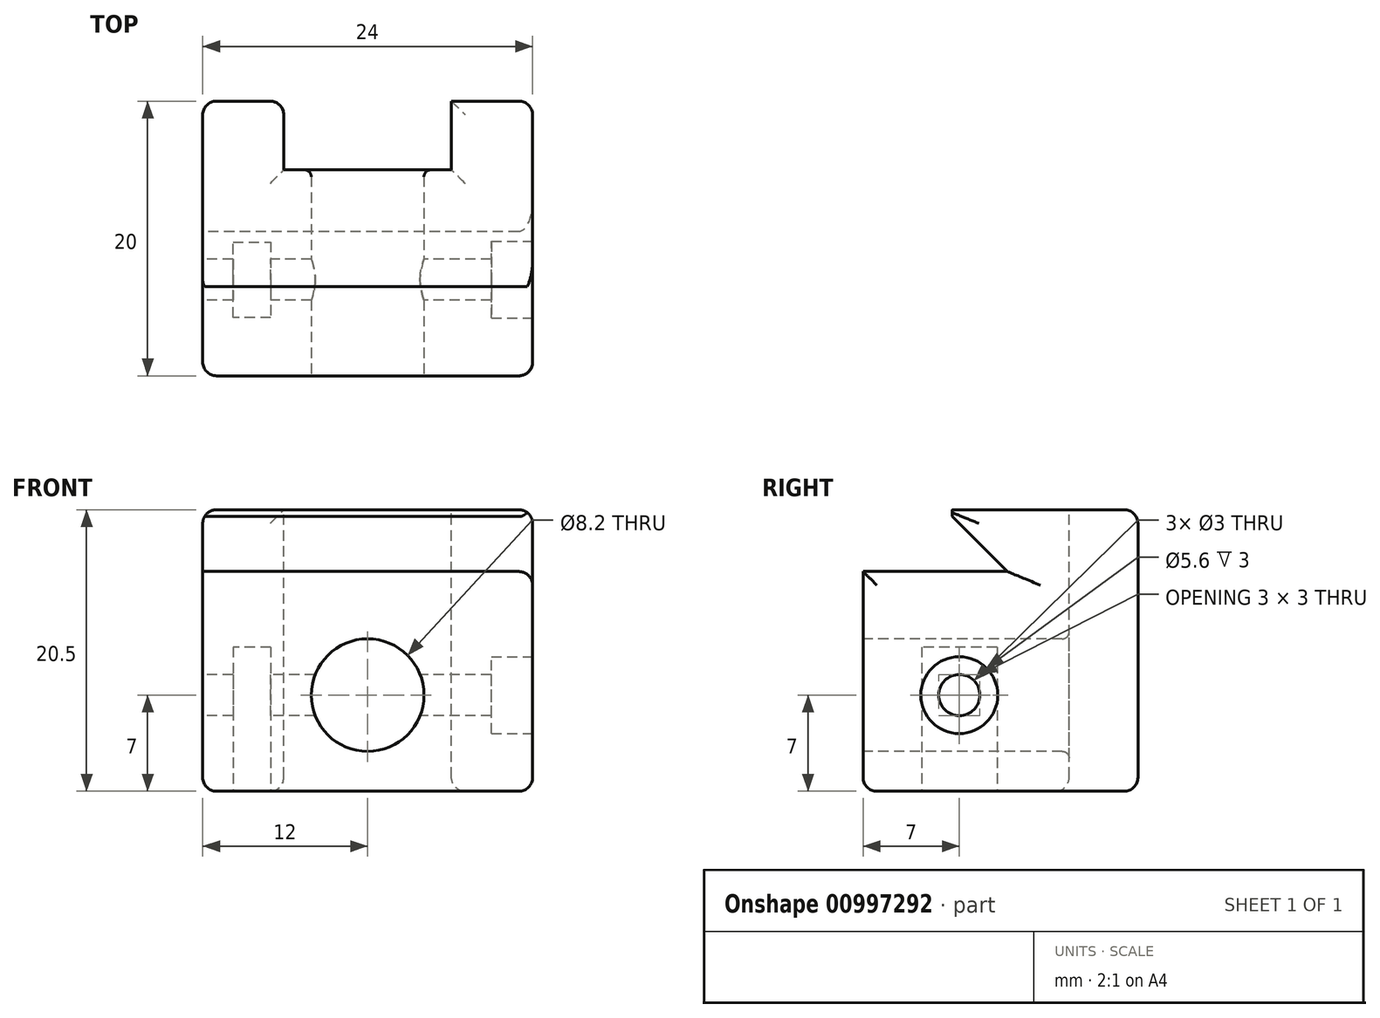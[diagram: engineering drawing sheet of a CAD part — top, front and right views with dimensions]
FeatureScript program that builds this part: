
annotation { "Feature Type Name" : "Feature", "Feature Type Description" : "" }
export const myFeature = defineFeature(function(context is Context, id is Id, definition is map)
    precondition{}
    {
        {
            var Q0;
            Q0=qCreatedBy(makeId("Top.planeOp"),FACE);
            var sketch = newSketch(context, id + "F0", { "sketchPlane" : qUnion([Q0])});
            skLineSegment(sketch, "E0.bottom", {"start": v(12, 10) * mm, "end": v(-12, 10) * mm});
            skLineSegment(sketch, "E0.top", {"start": v(12, -10) * mm, "end": v(-12, -10) * mm});
            skLineSegment(sketch, "E0.left", {"start": v(12, 10) * mm, "end": v(12, -10) * mm});
            skLineSegment(sketch, "E0.right", {"start": v(-12, 10) * mm, "end": v(-12, -10) * mm});
            skPoint(sketch, "E0.middle", {"position": v(0, 0) * mm});
            skSolve(sketch);
        }
        {
            var Q0;
            Q0 = qSketchRegion(id + "F0", true);
            extrude(context, id + "F1", {"entities" : qUnion([Q0]), "depth" : 18.5 * mm, "offsetDistance" : 25 * mm});
        }
        {
            var Q0;
            Q0=makeQuery(id+"F1.opExtrude","SWEPT_FACE",FACE,{"disambiguationData":[OSD([sQuery(id+"F0.wireOp",EDGE,"E0.right")])]});
            var sketch = newSketch(context, id + "F2", { "sketchPlane" : qUnion([Q0])});
            skLineSegment(sketch, "E1", {"start": v(10, 0) * mm, "end": v(10, 14) * mm, "construction": true});
            skLineSegment(sketch, "E2", {"start": v(10, 14) * mm, "end": v(-0.5, 14) * mm});
            skLineSegment(sketch, "E3", {"start": v(-10, 18.5) * mm, "end": v(4, 18.5) * mm, "construction": true});
            skLineSegment(sketch, "E4", {"start": v(3.5, 18) * mm, "end": v(-0.5, 14) * mm});
            skLineSegment(sketch, "E5", {"start": v(4, 18.5) * mm, "end": v(3.5, 18.5) * mm, "construction": true});
            skLineSegment(sketch, "E6", {"start": v(3.5, 18.5) * mm, "end": v(3.5, 18) * mm});
            skLineSegment(sketch, "E7", {"start": v(10, 0) * mm, "end": v(10, 5) * mm, "construction": true});
            skLineSegment(sketch, "E8", {"start": v(10, 5) * mm, "end": v(3, 5) * mm, "construction": true});
            skCircle(sketch, "E9", {"center": v(3, 5) * mm, "radius": 1.5 * mm});
            skSolve(sketch);
        }
        {
            var Q0;
            {var subQ4=sQuery(id+"F2.wireOp",EDGE,"E2");Q0=makeQuery(id+"F2.imprint","IMPRINT",FACE,{"disambiguationData":[TD([[makeQuery(id+"F2.imprint","IMPRINT",EDGE,{"derivedFrom":subQ4}),-1.0]])]});}
            var Q1;
            Q1=makeQuery(id+"F2.imprint","IMPRINT",FACE,{"disambiguationData":[TD([[makeQuery(id+"F2.imprint","IMPRINT",EDGE,{"derivedFrom":sQuery(id+"F2.wireOp",EDGE,"E9")}),1.0]])]});
            extrude(context, id + "F3", {"entities" : qUnion([Q0, Q1]), "operationType" : NewBodyOperationType.REMOVE, "oppositeDirection" : true, "depth" : 25 * mm, "offsetDistance" : 25 * mm});
        }
        {
            var Q0;
            Q0=makeQuery(id+"F1.opExtrude","CAP_FACE",FACE,{"disambiguationData":[OSD([sQuery(id+"F0.wireOp",EDGE,"E0.bottom"),sQuery(id+"F0.wireOp",EDGE,"E0.top"),sQuery(id+"F0.wireOp",EDGE,"E0.left"),sQuery(id+"F0.wireOp",EDGE,"E0.right")])],"isStart":true});
            extrude(context, id + "F4", {"entities" : qUnion([Q0]), "operationType" : NewBodyOperationType.ADD, "depth" : 2 * mm, "offsetDistance" : 25 * mm});
        }
        {
            var Q0;
            {var subQ0=sQuery(id+"F0.wireOp",EDGE,"E0.top");Q0=makeQuery(id+"F4.boolean.opBoolean","MERGE",FACE,{"derivedFrom":[makeQuery(id+"F1.opExtrude","SWEPT_FACE",FACE,{"disambiguationData":[OSD([subQ0])]}),makeQuery(id+"F4.opExtrude","SWEPT_FACE",FACE,{"disambiguationData":[OSD([subQ0])]})]});}
            var sketch = newSketch(context, id + "F5", { "sketchPlane" : qUnion([Q0])});
            skLineSegment(sketch, "E10", {"start": v(0, -2) * mm, "end": v(0, 12) * mm, "construction": true});
            skCircle(sketch, "E11", {"center": v(0, 5) * mm, "radius": 4.1 * mm});
            skSolve(sketch);
        }
        {
            var Q0;
            Q0=makeQuery(id+"F5.imprint","IMPRINT",FACE,{"disambiguationData":[TD([[makeQuery(id+"F5.imprint","IMPRINT",EDGE,{"derivedFrom":sQuery(id+"F5.wireOp",EDGE,"E11")}),1.0]])]});
            extrude(context, id + "F6", {"entities" : qUnion([Q0]), "operationType" : NewBodyOperationType.REMOVE, "oppositeDirection" : true, "depth" : 25 * mm, "offsetDistance" : 25 * mm});
        }
        {
            var Q0;
            Q0=makeQuery(id+"F1.opExtrude","CAP_FACE",FACE,{"disambiguationData":[OSD([sQuery(id+"F0.wireOp",EDGE,"E0.bottom"),sQuery(id+"F0.wireOp",EDGE,"E0.top"),sQuery(id+"F0.wireOp",EDGE,"E0.left"),sQuery(id+"F0.wireOp",EDGE,"E0.right")])],"isStart":false});
            var sketch = newSketch(context, id + "F7", { "sketchPlane" : qUnion([Q0])});
            skLineSegment(sketch, "E12", {"start": v(0, 10) * mm, "end": v(6.1, 10) * mm, "construction": true});
            skLineSegment(sketch, "E13", {"start": v(0, 10) * mm, "end": v(-6.1, 10) * mm, "construction": true});
            skLineSegment(sketch, "E14", {"start": v(-6.1, 10) * mm, "end": v(-6.1, 5) * mm});
            skLineSegment(sketch, "E15", {"start": v(-6.1, 5) * mm, "end": v(6.1, 5) * mm});
            skLineSegment(sketch, "E16", {"start": v(6.1, 5) * mm, "end": v(6.1, 10) * mm});
            skSolve(sketch);
        }
        {
            var Q0;
            {var subQ0=sQuery(id+"F7.wireOp",EDGE,"E14");Q0=makeQuery(id+"F7.imprint","IMPRINT",FACE,{"disambiguationData":[TD([[makeQuery(id+"F7.imprint","IMPRINT",EDGE,{"derivedFrom":subQ0}),1.0]])]});}
            extrude(context, id + "F8", {"entities" : qUnion([Q0]), "operationType" : NewBodyOperationType.REMOVE, "oppositeDirection" : true, "depth" : 25 * mm, "offsetDistance" : 25 * mm});
        }
        {
            var Q0;
            {var subQ0=sQuery(id+"F0.wireOp",EDGE,"E0.left");Q0=makeQuery(id+"F4.boolean.opBoolean","MERGE",FACE,{"derivedFrom":[makeQuery(id+"F1.opExtrude","SWEPT_FACE",FACE,{"disambiguationData":[OSD([subQ0])]}),makeQuery(id+"F4.opExtrude","SWEPT_FACE",FACE,{"disambiguationData":[OSD([subQ0])]})]});}
            var sketch = newSketch(context, id + "F9", { "sketchPlane" : qUnion([Q0])});
            skCircle(sketch, "E17", {"center": v(-3, 5) * mm, "radius": 2.8 * mm});
            skSolve(sketch);
        }
        {
            var Q0;
            Q0=makeQuery(id+"F9.imprint","IMPRINT",FACE,{"disambiguationData":[TD([[makeQuery(id+"F9.imprint","IMPRINT",EDGE,{"derivedFrom":sQuery(id+"F9.wireOp",EDGE,"E17")}),1.0]])]});
            extrude(context, id + "F10", {"entities" : qUnion([Q0]), "operationType" : NewBodyOperationType.REMOVE, "oppositeDirection" : true, "depth" : 3 * mm, "offsetDistance" : 25 * mm});
        }
        {
            var Q0;
            Q0=makeQuery(id+"F4.opExtrude","CAP_FACE",FACE,{"disambiguationData":[OSD([sQuery(id+"F0.wireOp",EDGE,"E0.bottom"),sQuery(id+"F0.wireOp",EDGE,"E0.top"),sQuery(id+"F0.wireOp",EDGE,"E0.left"),sQuery(id+"F0.wireOp",EDGE,"E0.right")])],"isStart":false});
            var sketch = newSketch(context, id + "F11", { "sketchPlane" : qUnion([Q0])});
            skLineSegment(sketch, "E18", {"start": v(0, 10) * mm, "end": v(0, 3) * mm, "construction": true});
            skLineSegment(sketch, "E19", {"start": v(0, 3) * mm, "end": v(-7.05, 3) * mm, "construction": true});
            skLineSegment(sketch, "E20", {"start": v(-7.05, 3) * mm, "end": v(-7.05, 5.75) * mm});
            skLineSegment(sketch, "E21", {"start": v(-7.05, 5.75) * mm, "end": v(-9.8, 5.75) * mm});
            skLineSegment(sketch, "E22", {"start": v(-9.8, 5.75) * mm, "end": v(-9.8, 0.25) * mm});
            skLineSegment(sketch, "E23", {"start": v(-9.8, 0.25) * mm, "end": v(-7.05, 0.25) * mm});
            skLineSegment(sketch, "E24", {"start": v(-7.05, 0.25) * mm, "end": v(-7.05, 3) * mm});
            skLineSegment(sketch, "E25", {"start": v(-9.8, 3) * mm, "end": v(-12, 3) * mm, "construction": true});
            skSolve(sketch);
        }
        {
            var Q0;
            Q0=makeQuery(id+"F11.imprint","IMPRINT",FACE,{"disambiguationData":[TD([[makeQuery(id+"F11.imprint","IMPRINT",EDGE,{"derivedFrom":sQuery(id+"F11.wireOp",EDGE,"E20")}),1.0]])]});
            extrude(context, id + "F12", {"entities" : qUnion([Q0]), "operationType" : NewBodyOperationType.REMOVE, "oppositeDirection" : true, "depth" : 10.5 * mm, "offsetDistance" : 25 * mm});
        }
        {
            var Q0;
            Q0=makeQuery(id+"F3.boolean.opBoolean","COPY",EDGE,{"derivedFrom":makeQuery(id+"F3.opExtrude","CAP_EDGE",EDGE,{"disambiguationData":[OSD([sQuery(id+"F2.wireOp",EDGE,"E2")])],"isStart":true})});
            var Q1;
            Q1=makeQuery(id+"F3.boolean.opBoolean","COPY",EDGE,{"derivedFrom":makeQuery(id+"F3.opExtrude","SWEPT_EDGE",EDGE,{"disambiguationData":[OSD([sQuery(id+"F0.wireOp",EDGE,"E0.top"),sQuery(id+"F0.wireOp",EDGE,"E0.right"),sQuery(id+"F2.wireOp",EDGE,"E2")])]})});
            var Q2;
            Q2=makeQuery(id+"F3.boolean.opBoolean","INTERSECT",EDGE,{"derivedFrom":[makeQuery(id+"F1.opExtrude","SWEPT_FACE",FACE,{"disambiguationData":[OSD([sQuery(id+"F0.wireOp",EDGE,"E0.left")])]}),makeQuery(id+"F3.opExtrude","SWEPT_FACE",FACE,{"disambiguationData":[OSD([sQuery(id+"F2.wireOp",EDGE,"E2")])]})]});
            var Q3;
            Q3=makeQuery(id+"F3.boolean.opBoolean","INTERSECT",EDGE,{"derivedFrom":[makeQuery(id+"F1.opExtrude","SWEPT_FACE",FACE,{"disambiguationData":[OSD([sQuery(id+"F0.wireOp",EDGE,"E0.left")])]}),makeQuery(id+"F3.opExtrude","SWEPT_FACE",FACE,{"disambiguationData":[OSD([sQuery(id+"F2.wireOp",EDGE,"E4")])]})]});
            var Q4;
            Q4=makeQuery(id+"F3.boolean.opBoolean","COPY",EDGE,{"derivedFrom":makeQuery(id+"F3.opExtrude","CAP_EDGE",EDGE,{"disambiguationData":[OSD([sQuery(id+"F2.wireOp",EDGE,"E4")])],"isStart":true})});
            var Q5;
            Q5=makeQuery(id+"F1.opExtrude","CAP_EDGE",EDGE,{"disambiguationData":[OSD([sQuery(id+"F0.wireOp",EDGE,"E0.right")])],"isStart":false});
            var Q6;
            Q6=makeQuery(id+"F1.opExtrude","CAP_EDGE",EDGE,{"disambiguationData":[OSD([sQuery(id+"F0.wireOp",EDGE,"E0.left")])],"isStart":false});
            var Q7;
            {var subQ0=sQuery(id+"F0.wireOp",EDGE,"E0.left");var subQ1=sQuery(id+"F0.wireOp",EDGE,"E0.bottom");Q7=makeQuery(id+"F4.boolean.opBoolean","MERGE",EDGE,{"derivedFrom":[makeQuery(id+"F1.opExtrude","SWEPT_EDGE",EDGE,{"disambiguationData":[OSD([subQ1,subQ0])]}),makeQuery(id+"F4.opExtrude","SWEPT_EDGE",EDGE,{"disambiguationData":[OSD([subQ1,subQ0])]})]});}
            var Q8;
            {var subQ0=sQuery(id+"F0.wireOp",EDGE,"E0.left");var subQ1=sQuery(id+"F0.wireOp",EDGE,"E0.bottom");Q8=makeQuery(id+"F8.boolean.opBoolean","SPLIT",EDGE,{"disambiguationData":[TD([makeQuery(id+"F1.opExtrude","SWEPT_FACE",FACE,{"disambiguationData":[OSD([subQ0])]})])],"derivedFrom":makeQuery(id+"F1.opExtrude","CAP_EDGE",EDGE,{"disambiguationData":[OSD([subQ1])],"isStart":false})});}
            var Q9;
            {var subQ0=sQuery(id+"F0.wireOp",EDGE,"E0.right");var subQ1=sQuery(id+"F0.wireOp",EDGE,"E0.top");Q9=makeQuery(id+"F4.boolean.opBoolean","MERGE",EDGE,{"derivedFrom":[makeQuery(id+"F1.opExtrude","SWEPT_EDGE",EDGE,{"disambiguationData":[OSD([subQ1,subQ0])]}),makeQuery(id+"F4.opExtrude","SWEPT_EDGE",EDGE,{"disambiguationData":[OSD([subQ1,subQ0])]})]});}
            var Q10;
            {var subQ0=sQuery(id+"F0.wireOp",EDGE,"E0.left");var subQ1=sQuery(id+"F0.wireOp",EDGE,"E0.top");Q10=makeQuery(id+"F4.boolean.opBoolean","MERGE",EDGE,{"derivedFrom":[makeQuery(id+"F1.opExtrude","SWEPT_EDGE",EDGE,{"disambiguationData":[OSD([subQ1,subQ0])]}),makeQuery(id+"F4.opExtrude","SWEPT_EDGE",EDGE,{"disambiguationData":[OSD([subQ1,subQ0])]})]});}
            var Q11;
            {var subQ0=sQuery(id+"F0.wireOp",EDGE,"E0.right");var subQ1=sQuery(id+"F0.wireOp",EDGE,"E0.bottom");Q11=makeQuery(id+"F8.boolean.opBoolean","SPLIT",EDGE,{"disambiguationData":[TD([makeQuery(id+"F1.opExtrude","SWEPT_FACE",FACE,{"disambiguationData":[OSD([subQ0])]})])],"derivedFrom":makeQuery(id+"F1.opExtrude","CAP_EDGE",EDGE,{"disambiguationData":[OSD([subQ1])],"isStart":false})});}
            var Q12;
            Q12=makeQuery(id+"F8.boolean.opBoolean","COPY",EDGE,{"derivedFrom":makeQuery(id+"F8.opExtrude","CAP_EDGE",EDGE,{"disambiguationData":[OSD([sQuery(id+"F7.wireOp",EDGE,"E14")])],"isStart":true})});
            var Q13;
            Q13=makeQuery(id+"F8.boolean.opBoolean","COPY",EDGE,{"derivedFrom":makeQuery(id+"F8.opExtrude","CAP_EDGE",EDGE,{"disambiguationData":[OSD([sQuery(id+"F7.wireOp",EDGE,"E15")])],"isStart":true})});
            var Q14;
            Q14=makeQuery(id+"F8.boolean.opBoolean","COPY",EDGE,{"derivedFrom":makeQuery(id+"F8.opExtrude","CAP_EDGE",EDGE,{"disambiguationData":[OSD([sQuery(id+"F7.wireOp",EDGE,"E16")])],"isStart":true})});
            var Q15;
            Q15=makeQuery(id+"F8.boolean.opBoolean","COPY",EDGE,{"derivedFrom":makeQuery(id+"F8.opExtrude","SWEPT_EDGE",EDGE,{"disambiguationData":[OSD([sQuery(id+"F0.wireOp",EDGE,"E0.bottom"),sQuery(id+"F7.wireOp",EDGE,"E16")])]})});
            var Q16;
            Q16=makeQuery(id+"F8.boolean.opBoolean","COPY",EDGE,{"derivedFrom":makeQuery(id+"F8.opExtrude","SWEPT_EDGE",EDGE,{"disambiguationData":[OSD([sQuery(id+"F0.wireOp",EDGE,"E0.bottom"),sQuery(id+"F7.wireOp",EDGE,"E14")])]})});
            var Q17;
            {var subQ0=sQuery(id+"F0.wireOp",EDGE,"E0.right");var subQ1=sQuery(id+"F0.wireOp",EDGE,"E0.bottom");Q17=makeQuery(id+"F4.boolean.opBoolean","MERGE",EDGE,{"derivedFrom":[makeQuery(id+"F1.opExtrude","SWEPT_EDGE",EDGE,{"disambiguationData":[OSD([subQ1,subQ0])]}),makeQuery(id+"F4.opExtrude","SWEPT_EDGE",EDGE,{"disambiguationData":[OSD([subQ1,subQ0])]})]});}
            var Q18;
            {var subQ0=sQuery(id+"F0.wireOp",EDGE,"E0.left");var subQ1=sQuery(id+"F0.wireOp",EDGE,"E0.bottom");Q18=makeQuery(id+"F8.boolean.opBoolean","SPLIT",EDGE,{"disambiguationData":[TD([makeQuery(id+"F1.opExtrude","SWEPT_FACE",FACE,{"disambiguationData":[OSD([subQ0])]})])],"derivedFrom":makeQuery(id+"F4.opExtrude","CAP_EDGE",EDGE,{"disambiguationData":[OSD([subQ1])],"isStart":false})});}
            var Q19;
            {var subQ0=sQuery(id+"F0.wireOp",EDGE,"E0.right");var subQ1=sQuery(id+"F0.wireOp",EDGE,"E0.bottom");Q19=makeQuery(id+"F8.boolean.opBoolean","SPLIT",EDGE,{"disambiguationData":[TD([makeQuery(id+"F1.opExtrude","SWEPT_FACE",FACE,{"disambiguationData":[OSD([subQ0])]})])],"derivedFrom":makeQuery(id+"F4.opExtrude","CAP_EDGE",EDGE,{"disambiguationData":[OSD([subQ1])],"isStart":false})});}
            var Q20;
            Q20=makeQuery(id+"F8.boolean.opBoolean","INTERSECT",EDGE,{"derivedFrom":[makeQuery(id+"F4.opExtrude","CAP_FACE",FACE,{"disambiguationData":[OSD([sQuery(id+"F0.wireOp",EDGE,"E0.bottom"),sQuery(id+"F0.wireOp",EDGE,"E0.top"),sQuery(id+"F0.wireOp",EDGE,"E0.left"),sQuery(id+"F0.wireOp",EDGE,"E0.right")])],"isStart":false}),makeQuery(id+"F8.opExtrude","SWEPT_FACE",FACE,{"disambiguationData":[OSD([sQuery(id+"F7.wireOp",EDGE,"E14")])]})]});
            var Q21;
            Q21=makeQuery(id+"F8.boolean.opBoolean","INTERSECT",EDGE,{"derivedFrom":[makeQuery(id+"F4.opExtrude","CAP_FACE",FACE,{"disambiguationData":[OSD([sQuery(id+"F0.wireOp",EDGE,"E0.bottom"),sQuery(id+"F0.wireOp",EDGE,"E0.top"),sQuery(id+"F0.wireOp",EDGE,"E0.left"),sQuery(id+"F0.wireOp",EDGE,"E0.right")])],"isStart":false}),makeQuery(id+"F8.opExtrude","SWEPT_FACE",FACE,{"disambiguationData":[OSD([sQuery(id+"F7.wireOp",EDGE,"E15")])]})]});
            var Q22;
            Q22=makeQuery(id+"F8.boolean.opBoolean","INTERSECT",EDGE,{"derivedFrom":[makeQuery(id+"F4.opExtrude","CAP_FACE",FACE,{"disambiguationData":[OSD([sQuery(id+"F0.wireOp",EDGE,"E0.bottom"),sQuery(id+"F0.wireOp",EDGE,"E0.top"),sQuery(id+"F0.wireOp",EDGE,"E0.left"),sQuery(id+"F0.wireOp",EDGE,"E0.right")])],"isStart":false}),makeQuery(id+"F8.opExtrude","SWEPT_FACE",FACE,{"disambiguationData":[OSD([sQuery(id+"F7.wireOp",EDGE,"E16")])]})]});
            var Q23;
            Q23=makeQuery(id+"F4.opExtrude","CAP_EDGE",EDGE,{"disambiguationData":[OSD([sQuery(id+"F0.wireOp",EDGE,"E0.left")])],"isStart":false});
            var Q24;
            Q24=makeQuery(id+"F4.opExtrude","CAP_EDGE",EDGE,{"disambiguationData":[OSD([sQuery(id+"F0.wireOp",EDGE,"E0.right")])],"isStart":false});
            var Q25;
            Q25=makeQuery(id+"F4.opExtrude","CAP_EDGE",EDGE,{"disambiguationData":[OSD([sQuery(id+"F0.wireOp",EDGE,"E0.top")])],"isStart":false});
            var Q26;
            Q26=makeQuery(id+"F12.boolean.opBoolean","COPY",EDGE,{"derivedFrom":makeQuery(id+"F12.opExtrude","CAP_EDGE",EDGE,{"disambiguationData":[OSD([sQuery(id+"F11.wireOp",EDGE,"E23")])],"isStart":true})});
            var Q27;
            Q27=makeQuery(id+"F12.boolean.opBoolean","COPY",EDGE,{"derivedFrom":makeQuery(id+"F12.opExtrude","CAP_EDGE",EDGE,{"disambiguationData":[OSD([sQuery(id+"F11.wireOp",EDGE,"E22")])],"isStart":true})});
            var Q28;
            Q28=makeQuery(id+"F12.boolean.opBoolean","COPY",EDGE,{"derivedFrom":makeQuery(id+"F12.opExtrude","CAP_EDGE",EDGE,{"disambiguationData":[OSD([sQuery(id+"F11.wireOp",EDGE,"E20"),sQuery(id+"F11.wireOp",EDGE,"E24")])],"isStart":true})});
            var Q29;
            Q29=makeQuery(id+"F12.boolean.opBoolean","COPY",EDGE,{"derivedFrom":makeQuery(id+"F12.opExtrude","CAP_EDGE",EDGE,{"disambiguationData":[OSD([sQuery(id+"F11.wireOp",EDGE,"E21")])],"isStart":true})});
            fillet(context, id + "F13", {"entities" : qUnion([Q0, Q1, Q2, Q3, Q4, Q5, Q6, Q7, Q8, Q9, Q10, Q11, Q12, Q13, Q14, Q15, Q16, Q17, Q18, Q19, Q20, Q21, Q22, Q23, Q24, Q25, Q26, Q27, Q28, Q29]), "radius" : 1 * mm, "tangentPropagation" : true, "allowEdgeOverflow" : false});
        }
        {
            var Q0;
            Q0=makeQuery(id+"F10.boolean.opBoolean","COPY",EDGE,{"derivedFrom":makeQuery(id+"F10.opExtrude","CAP_EDGE",EDGE,{"disambiguationData":[OSD([sQuery(id+"F9.wireOp",EDGE,"E17")])],"isStart":true})});
            var Q1;
            Q1=makeQuery(id+"F6.boolean.opBoolean","COPY",EDGE,{"derivedFrom":makeQuery(id+"F6.opExtrude","CAP_EDGE",EDGE,{"disambiguationData":[OSD([sQuery(id+"F5.wireOp",EDGE,"E11")])],"isStart":true})});
            var Q2;
            Q2=makeQuery(id+"F8.boolean.opBoolean","INTERSECT",EDGE,{"derivedFrom":[makeQuery(id+"F6.boolean.opBoolean","COPY",FACE,{"derivedFrom":makeQuery(id+"F6.opExtrude","SWEPT_FACE",FACE,{"disambiguationData":[OSD([sQuery(id+"F5.wireOp",EDGE,"E11")])]})}),makeQuery(id+"F8.opExtrude","SWEPT_FACE",FACE,{"disambiguationData":[OSD([sQuery(id+"F7.wireOp",EDGE,"E15")])]})]});
            var Q3;
            Q3=makeQuery(id+"F3.boolean.opBoolean","COPY",EDGE,{"derivedFrom":makeQuery(id+"F3.opExtrude","CAP_EDGE",EDGE,{"disambiguationData":[OSD([sQuery(id+"F2.wireOp",EDGE,"E9")])],"isStart":true})});
            var Q4;
            Q4=makeQuery(id+"F10.boolean.opBoolean","COPY",EDGE,{"derivedFrom":makeQuery(id+"F10.opExtrude","CAP_EDGE",EDGE,{"disambiguationData":[OSD([sQuery(id+"F0.wireOp",EDGE,"E0.left"),sQuery(id+"F2.wireOp",EDGE,"E9")])],"isStart":false})});
            fillet(context, id + "F14", {"entities" : qUnion([Q0, Q1, Q2, Q3, Q4]), "radius" : .5 * mm, "tangentPropagation" : true, "allowEdgeOverflow" : false});
        }
    });
